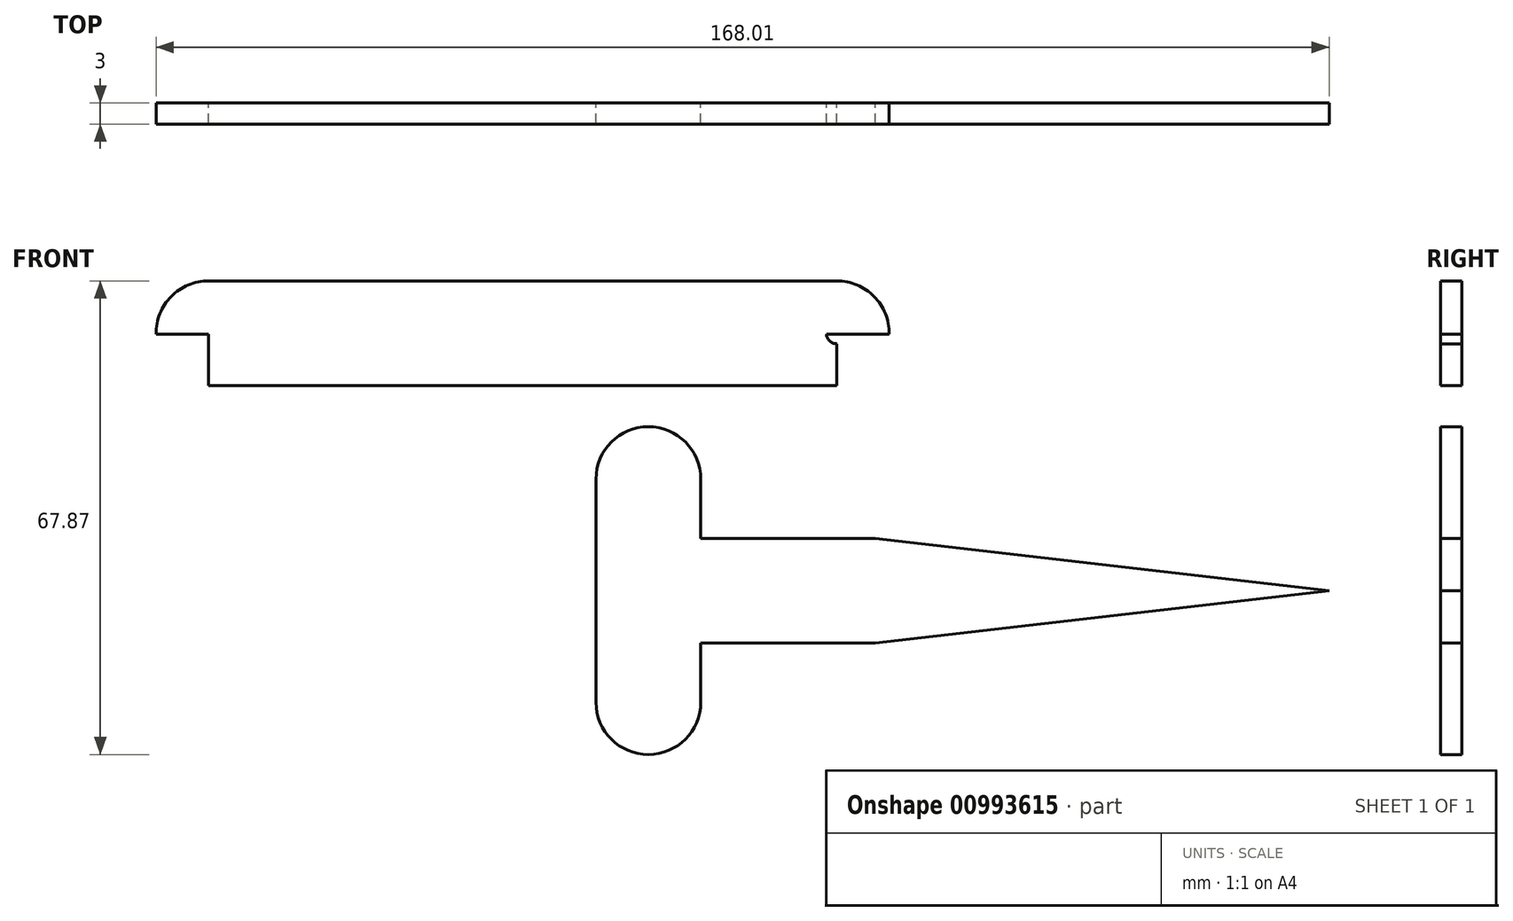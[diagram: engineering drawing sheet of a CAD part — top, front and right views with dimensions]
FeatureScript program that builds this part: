
annotation { "Feature Type Name" : "Feature", "Feature Type Description" : "" }
export const myFeature = defineFeature(function(context is Context, id is Id, definition is map)
    precondition{}
    {
        {
            var Q0;
            Q0=qCreatedBy(makeId("Front.planeOp"),FACE);
            var sketch = newSketch(context, id + "F0", { "sketchPlane" : qUnion([Q0])});
            skLineSegment(sketch, "E0.bottom", {"start": v(-70.5, 36.87) * mm, "end": v(19.5, 36.87) * mm});
            skLineSegment(sketch, "E0.top", {"start": v(-70.5, 51.87) * mm, "end": v(19.5, 51.87) * mm});
            skLineSegment(sketch, "E0.left", {"start": v(-70.5, 36.87) * mm, "end": v(-70.5, 51.87) * mm});
            skLineSegment(sketch, "E0.right", {"start": v(19.5, 36.87) * mm, "end": v(19.5, 51.87) * mm});
            skArc(sketch, "E1", {"start": v(19.5, 36.87) * mm, "mid": v(27, 44.37) * mm, "end": v(19.5, 51.87) * mm});
            skArc(sketch, "E2", {"start": v(-70.5, 51.87) * mm, "mid": v(-78, 44.37) * mm, "end": v(-70.5, 36.87) * mm});
            skLineSegment(sketch, "E3.left", {"start": v(0, 0) * mm, "end": v(0, 15) * mm});
            skLineSegment(sketch, "E4", {"start": v(25, 15) * mm, "end": v(90, 7.5) * mm});
            skLineSegment(sketch, "E5", {"start": v(25, 0) * mm, "end": v(90, 7.5) * mm});
            skLineSegment(sketch, "E6", {"start": v(0, 0) * mm, "end": v(25, 0) * mm});
            skLineSegment(sketch, "E7", {"start": v(0, 15) * mm, "end": v(25, 15) * mm});
            skCircle(sketch, "E8", {"center": v(19.5, 44.37) * mm, "radius": 1.5 * mm});
            skLineSegment(sketch, "E9", {"start": v(-59.82, 44.27) * mm, "end": v(-78, 44.27) * mm});
            skLineSegment(sketch, "E10", {"start": v(-59.82, 44.27) * mm, "end": v(27, 44.27) * mm});
            skLineSegment(sketch, "E11", {"start": v(-59.82, 44.27) * mm, "end": v(-59.82, 36.87) * mm, "construction": true});
            skLineSegment(sketch, "E12", {"start": v(0, 15) * mm, "end": v(0, 23.5) * mm});
            skLineSegment(sketch, "E13", {"start": v(0, 0) * mm, "end": v(0, -8.5) * mm});
            skLineSegment(sketch, "E14", {"start": v(0, 15) * mm, "end": v(-15, 15) * mm});
            skLineSegment(sketch, "E15", {"start": v(-15, 15) * mm, "end": v(-15, 23.5) * mm});
            skArc(sketch, "E16", {"start": v(0, 23.5) * mm, "mid": v(-7.5, 31) * mm, "end": v(-15, 23.5) * mm});
            skLineSegment(sketch, "E17", {"start": v(0, 0) * mm, "end": v(-15, 0) * mm});
            skLineSegment(sketch, "E18", {"start": v(-15, 0) * mm, "end": v(-15, -8.5) * mm});
            skArc(sketch, "E19", {"start": v(-15, -8.5) * mm, "mid": v(-7.5, -16) * mm, "end": v(0, -8.5) * mm});
            skLineSegment(sketch, "E20", {"start": v(-15, 15) * mm, "end": v(-15, 0) * mm});
            skCircle(sketch, "E21", {"center": v(-7.5, 23.5) * mm, "radius": 1.5 * mm});
            skCircle(sketch, "E22", {"center": v(-7.5, -8.5) * mm, "radius": 1.5 * mm});
            skSolve(sketch);
        }
        {
            var Q0;
            Q0=makeQuery(id+"F0.imprint","IMPRINT",FACE,{"disambiguationData":[TD([[makeQuery(id+"F0.imprint","IMPRINT",EDGE,{"derivedFrom":sQuery(id+"F0.wireOp",EDGE,"E3.left")}),1.0]])]});
            var Q1;
            Q1=makeQuery(id+"F0.imprint","IMPRINT",FACE,{"disambiguationData":[TD([[makeQuery(id+"F0.imprint","IMPRINT",EDGE,{"derivedFrom":sQuery(id+"F0.wireOp",EDGE,"E12")}),1.0]])]});
            var Q2;
            Q2=makeQuery(id+"F0.imprint","IMPRINT",FACE,{"disambiguationData":[TD([[makeQuery(id+"F0.imprint","IMPRINT",EDGE,{"derivedFrom":sQuery(id+"F0.wireOp",EDGE,"E21")}),1.0]])]});
            var Q3;
            Q3=makeQuery(id+"F0.imprint","IMPRINT",FACE,{"disambiguationData":[TD([[makeQuery(id+"F0.imprint","IMPRINT",EDGE,{"derivedFrom":sQuery(id+"F0.wireOp",EDGE,"E13")}),-1.0]])]});
            var Q4;
            Q4=makeQuery(id+"F0.imprint","IMPRINT",FACE,{"disambiguationData":[TD([[makeQuery(id+"F0.imprint","IMPRINT",EDGE,{"derivedFrom":sQuery(id+"F0.wireOp",EDGE,"E3.left")}),-1.0]])]});
            var Q5;
            Q5=makeQuery(id+"F0.imprint","IMPRINT",FACE,{"disambiguationData":[TD([[makeQuery(id+"F0.imprint","IMPRINT",EDGE,{"derivedFrom":sQuery(id+"F0.wireOp",EDGE,"E22")}),1.0]])]});
            var Q6;
            {var subQ1=sQuery(id+"F0.wireOp",EDGE,"E0.left");var subQ3=sQuery(id+"F0.wireOp",EDGE,"tS127I62-a7ML-rPey-h6fs-zSG0eudvvqb0");var subQ4=makeQuery(id+"F0.imprint","INTERSECT",VERTEX,{"disambiguationData":[OD(1.0)],"derivedFrom":[subQ1,subQ3]});Q6=makeQuery(id+"F0.imprint","IMPRINT",FACE,{"disambiguationData":[TD([[makeQuery(id+"F0.imprint","IMPRINT",EDGE,{"disambiguationData":[TD([[subQ4,-1.0]])],"derivedFrom":subQ3}),-1.0]])]});}
            var Q7;
            {var subQ6=sQuery(id+"F0.wireOp",EDGE,"E0.bottom");Q7=makeQuery(id+"F0.imprint","IMPRINT",FACE,{"disambiguationData":[TD([[makeQuery(id+"F0.imprint","IMPRINT",EDGE,{"derivedFrom":subQ6}),1.0]])]});}
            var Q8;
            {var subQ6=sQuery(id+"F0.wireOp",EDGE,"E0.top");Q8=makeQuery(id+"F0.imprint","IMPRINT",FACE,{"disambiguationData":[TD([[makeQuery(id+"F0.imprint","IMPRINT",EDGE,{"derivedFrom":subQ6}),-1.0]])]});}
            var Q9;
            {var subQ1=sQuery(id+"F0.wireOp",EDGE,"E0.left");var subQ3=sQuery(id+"F0.wireOp",EDGE,"tS127I62-a7ML-rPey-h6fs-zSG0eudvvqb0");var subQ4=makeQuery(id+"F0.imprint","INTERSECT",VERTEX,{"disambiguationData":[OD(0.0)],"derivedFrom":[subQ1,subQ3]});Q9=makeQuery(id+"F0.imprint","IMPRINT",FACE,{"disambiguationData":[TD([[makeQuery(id+"F0.imprint","IMPRINT",EDGE,{"disambiguationData":[TD([[subQ4,1.0]])],"derivedFrom":subQ3}),-1.0]])]});}
            var Q10;
            {var subQ1=sQuery(id+"F0.wireOp",EDGE,"E0.right");var subQ3=sQuery(id+"F0.wireOp",EDGE,"E8");var subQ4=makeQuery(id+"F0.imprint","INTERSECT",VERTEX,{"disambiguationData":[OD(0.0)],"derivedFrom":[subQ1,subQ3]});Q10=makeQuery(id+"F0.imprint","IMPRINT",FACE,{"disambiguationData":[TD([[makeQuery(id+"F0.imprint","IMPRINT",EDGE,{"disambiguationData":[TD([[subQ4,-1.0]])],"derivedFrom":subQ3}),-1.0]])]});}
            var Q11;
            {var subQ1=sQuery(id+"F0.wireOp",EDGE,"E0.right");var subQ3=sQuery(id+"F0.wireOp",EDGE,"E8");var subQ4=makeQuery(id+"F0.imprint","INTERSECT",VERTEX,{"disambiguationData":[OD(1.0)],"derivedFrom":[subQ1,subQ3]});Q11=makeQuery(id+"F0.imprint","IMPRINT",FACE,{"disambiguationData":[TD([[makeQuery(id+"F0.imprint","IMPRINT",EDGE,{"disambiguationData":[TD([[subQ4,1.0]])],"derivedFrom":subQ3}),-1.0]])]});}
            var Q12;
            {var subQ0=sQuery(id+"F0.wireOp",EDGE,"E9");var subQ1=sQuery(id+"F0.wireOp",EDGE,"E0.left");var subQ2=makeQuery(id+"F0.imprint","INTERSECT",VERTEX,{"derivedFrom":[subQ1,subQ0]});Q12=makeQuery(id+"F0.imprint","IMPRINT",FACE,{"disambiguationData":[TD([[makeQuery(id+"F0.imprint","IMPRINT",EDGE,{"disambiguationData":[TD([[subQ2,-1.0]])],"derivedFrom":subQ1}),-1.0]])]});}
            var Q13;
            {var subQ0=sQuery(id+"F0.wireOp",EDGE,"E10");var subQ1=sQuery(id+"F0.wireOp",EDGE,"E0.right");var subQ2=makeQuery(id+"F0.imprint","INTERSECT",VERTEX,{"derivedFrom":[subQ1,subQ0]});Q13=makeQuery(id+"F0.imprint","IMPRINT",FACE,{"disambiguationData":[TD([[makeQuery(id+"F0.imprint","IMPRINT",EDGE,{"disambiguationData":[TD([[subQ2,-1.0]])],"derivedFrom":subQ1}),-1.0]])]});}
            var Q14;
            {var subQ0=sQuery(id+"F0.wireOp",EDGE,"tS127I62-a7ML-rPey-h6fs-zSG0eudvvqb0");var subQ1=sQuery(id+"F0.wireOp",EDGE,"E0.left");var subQ2=makeQuery(id+"F0.imprint","INTERSECT",VERTEX,{"disambiguationData":[OD(0.0)],"derivedFrom":[subQ1,subQ0]});Q14=makeQuery(id+"F0.imprint","IMPRINT",FACE,{"disambiguationData":[TD([[makeQuery(id+"F0.imprint","IMPRINT",EDGE,{"disambiguationData":[TD([[subQ2,-1.0]])],"derivedFrom":subQ1}),-1.0]])]});}
            var Q15;
            {var subQ0=sQuery(id+"F0.wireOp",EDGE,"E10");var subQ1=sQuery(id+"F0.wireOp",EDGE,"E0.right");var subQ2=makeQuery(id+"F0.imprint","INTERSECT",VERTEX,{"derivedFrom":[subQ1,subQ0]});Q15=makeQuery(id+"F0.imprint","IMPRINT",FACE,{"disambiguationData":[TD([[makeQuery(id+"F0.imprint","IMPRINT",EDGE,{"disambiguationData":[TD([[subQ2,-1.0]])],"derivedFrom":subQ1}),1.0]])]});}
            var Q16;
            {var subQ0=sQuery(id+"F0.wireOp",EDGE,"tS127I62-a7ML-rPey-h6fs-zSG0eudvvqb0");var subQ1=sQuery(id+"F0.wireOp",EDGE,"E0.left");var subQ2=makeQuery(id+"F0.imprint","INTERSECT",VERTEX,{"disambiguationData":[OD(0.0)],"derivedFrom":[subQ1,subQ0]});Q16=makeQuery(id+"F0.imprint","IMPRINT",FACE,{"disambiguationData":[TD([[makeQuery(id+"F0.imprint","IMPRINT",EDGE,{"disambiguationData":[TD([[subQ2,-1.0]])],"derivedFrom":subQ1}),1.0]])]});}
            var Q17;
            {var subQ0=sQuery(id+"F0.wireOp",EDGE,"E8");var subQ1=sQuery(id+"F0.wireOp",EDGE,"E0.right");var subQ2=makeQuery(id+"F0.imprint","INTERSECT",VERTEX,{"disambiguationData":[OD(0.0)],"derivedFrom":[subQ1,subQ0]});Q17=makeQuery(id+"F0.imprint","IMPRINT",FACE,{"disambiguationData":[TD([[makeQuery(id+"F0.imprint","IMPRINT",EDGE,{"disambiguationData":[TD([[subQ2,-1.0]])],"derivedFrom":subQ1}),-1.0]])]});}
            var Q18;
            {var subQ0=sQuery(id+"F0.wireOp",EDGE,"E8");var subQ1=sQuery(id+"F0.wireOp",EDGE,"E0.right");var subQ2=makeQuery(id+"F0.imprint","INTERSECT",VERTEX,{"disambiguationData":[OD(0.0)],"derivedFrom":[subQ1,subQ0]});Q18=makeQuery(id+"F0.imprint","IMPRINT",FACE,{"disambiguationData":[TD([[makeQuery(id+"F0.imprint","IMPRINT",EDGE,{"disambiguationData":[TD([[subQ2,-1.0]])],"derivedFrom":subQ1}),1.0]])]});}
            var Q19;
            {var subQ0=sQuery(id+"F0.wireOp",EDGE,"E9");var subQ1=sQuery(id+"F0.wireOp",EDGE,"E0.left");var subQ2=makeQuery(id+"F0.imprint","INTERSECT",VERTEX,{"derivedFrom":[subQ1,subQ0]});Q19=makeQuery(id+"F0.imprint","IMPRINT",FACE,{"disambiguationData":[TD([[makeQuery(id+"F0.imprint","IMPRINT",EDGE,{"disambiguationData":[TD([[subQ2,-1.0]])],"derivedFrom":subQ1}),1.0]])]});}
            extrude(context, id + "F1", {"entities" : qUnion([Q0, Q1, Q2, Q3, Q4, Q5, Q6, Q7, Q8, Q9, Q10, Q11, Q12, Q13, Q14, Q15, Q16, Q17, Q18, Q19]), "depth" : 3 * mm, "offsetDistance" : 25 * mm});
        }
    });
